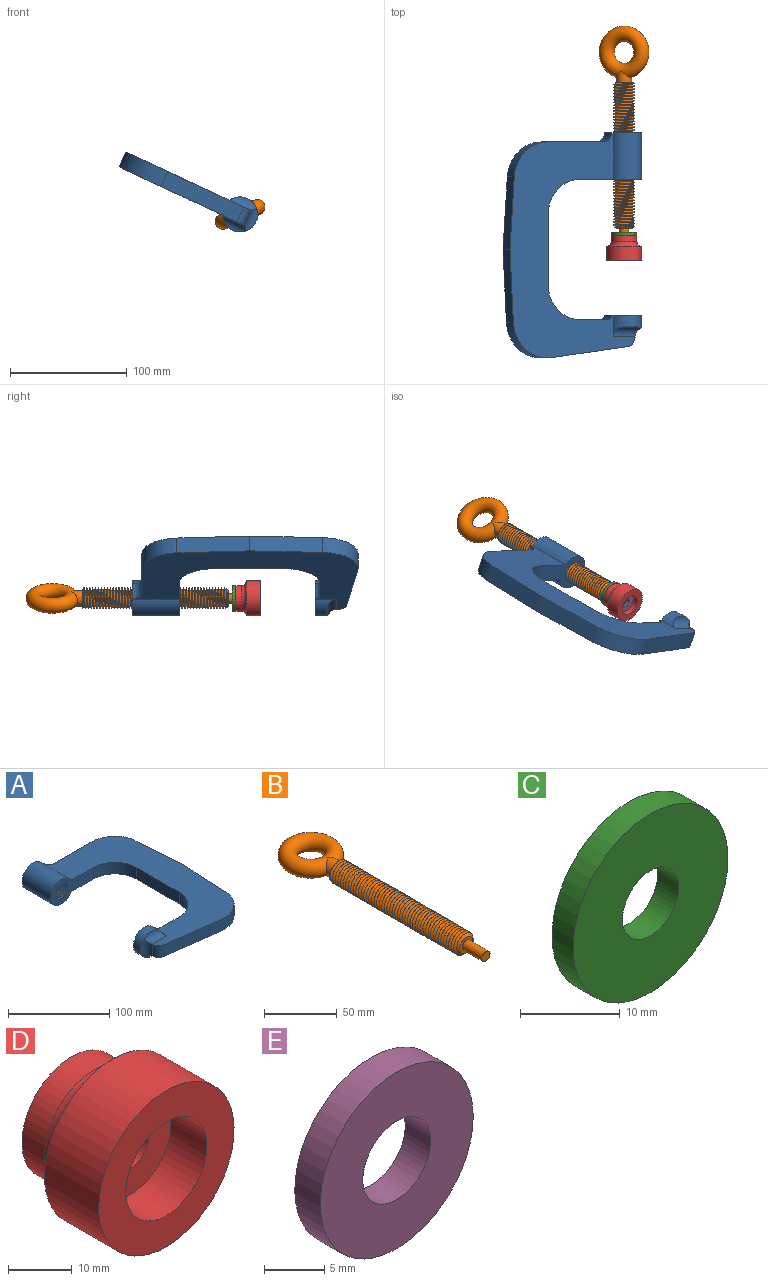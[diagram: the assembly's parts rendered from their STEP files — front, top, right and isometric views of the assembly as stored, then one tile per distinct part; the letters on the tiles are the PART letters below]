
ASSEMBLY  parts=5 mates=4
PART A: 26 faces, bbox 127.1x194.8x31.1 mm
  f0: cylinder r=15mm len=30mm, axis (0,1,0), area 973.5mm2, adj f5,f6,f7,f8,f24,f25
  f1: cylinder r=15mm len=40mm, axis (0,1,0), area 3187.3mm2, adj f3,f4,f7,f8
  f2: cylinder r=8mm len=14mm, axis (0,0,-1), area 168.5mm2, adj f6,f7,f8,f14
  f3: plane 61.09x31.09mm, normal (0,-1,0), area 911.6mm2, adj f1,f7,f8,f9,f21,f22,f23
  f4: plane 31.1x31.1mm, normal (0,1,0), area 491.6mm2, adj f1,f7,f8,f20,f21,f22,f23
  f5: plane 30x30mm, normal (0,1,0), area 714.8mm2, adj f0,f7,f8,f13
  f6: cylinder r=8mm len=21.21mm, axis (0,0,-1), area 206.8mm2, adj f0,f2,f7,f8,f24,f25
  f7: plane 192.73x118.03mm, normal (0,0,-1), area 10128.8mm2, adj f0,f1,f2,f3,f4,f5,f6,f9
  f8: plane 192.73x118.03mm, normal (0,0,1), area 10128.8mm2, adj f0,f1,f2,f3,f4,f5,f6,f9
  f9: cylinder r=30mm len=30mm, axis (0,0,-1), area 659.7mm2, adj f3,f7,f8,f10
  f10: plane 60x14mm, normal (-1,0,0), area 840mm2, adj f7,f8,f9,f11
  f11: cylinder r=30mm len=30mm, axis (0,0,-1), area 659.7mm2, adj f7,f8,f10,f12
  f12: plane 26x14mm, normal (0,1,0), area 364mm2, adj f7,f8,f11,f13
  f13: cylinder r=4mm len=14mm, axis (0,0,-1), area 88mm2, adj f5,f7,f8,f12
  f14: plane 71.71x14mm, normal (-0.13,-0.99,0), area 1012.7mm2, adj f2,f7,f8,f15
  f15: cylinder r=32mm len=36.15mm, axis (0,0,-1), area 739.5mm2, adj f7,f8,f14,f16
  f16: plane 62.38x14mm, normal (1,-0.05,0), area 874.5mm2, adj f7,f8,f15,f17
  f17: plane 62.08x14mm, normal (1,0.07,0), area 871mm2, adj f7,f8,f16,f18
  f18: cylinder r=32mm len=31.93mm, axis (0,0,-1), area 674.5mm2, adj f7,f8,f17,f19
  f19: plane 52.02x14mm, normal (0,1,0), area 728.3mm2, adj f7,f8,f18,f20
  f20: cylinder r=8mm len=14mm, axis (0,0,-1), area 175.9mm2, adj f4,f7,f8,f19
  f21: bspline ~41.89x16.58mm, area 1676.5mm2, adj f3,f4,f22,f23
  f22: bspline ~41.22x17.87mm, area 690.8mm2, adj f3,f4,f21,f23
  f23: bspline ~42.2x19.05mm, area 1678.2mm2, adj f3,f4,f21,f22
  f24: cylinder r=8mm len=23.87mm, axis (1,0,0), area 177.7mm2, adj f0,f6,f7
  f25: cylinder r=8mm len=23.87mm, axis (-1,0,0), area 177.7mm2, adj f0,f6,f8
PART B: 11 faces, bbox 50x195.7x19.3 mm
  f0: torus R=16mm, axis (0,0,-1), area 3935mm2, adj f1
  f1: cylinder r=6.5mm len=13mm, axis (0,-1,0), area 295.3mm2, adj f0,f5
  f2: cylinder r=4mm len=19mm, axis (0,-1,0), area 477.5mm2, adj f6,f7
  f3: cone r=6.5mm half-angle=45deg, axis (0,1,0), area 96.7mm2, adj f4,f7,f8,f9,f10
  f4: cylinder r=9mm len=122.5mm, axis (0,-1,0), area 168.2mm2, adj f3,f5,f9,f10
  f5: plane 17.36x17.33mm, normal (0,1,0), area 68.3mm2, adj f1,f4,f8,f9,f10
  f6: plane 8x8mm, normal (0,-1,0), area 50.3mm2, adj f2
  f7: plane 13x13mm, normal (0,-1,0), area 82.5mm2, adj f2,f3
  f8: bspline ~124.9x14.21mm, area 668.4mm2, adj f3,f5,f9,f10
  f9: bspline ~125.68x20.78mm, area 5481.3mm2, adj f3,f4,f5,f8
  f10: bspline ~126.93x20.78mm, area 5470.5mm2, adj f3,f4,f5,f8
PART C: 4 faces, bbox 22x3x22 mm
  f0: cylinder r=4mm len=8mm, axis (0,-1,0), area 75.4mm2, adj f2,f3
  f1: cylinder r=11mm len=22mm, axis (0,-1,0), area 207.3mm2, adj f2,f3
  f2: plane 22x22mm, normal (0,1,0), area 329.9mm2, adj f0,f1
  f3: plane 22x22mm, normal (0,-1,0), area 329.9mm2, adj f0,f1
PART D: 8 faces, bbox 32.5x21x32.5 mm
  f0: torus R=15mm, axis (0,-1,0), area 491.6mm2, adj f1,f4
  f1: cylinder r=15mm len=30mm, axis (0,-1,0), area 1131mm2, adj f0,f7
  f2: cylinder r=9mm len=18mm, axis (0,-1,0), area 452.4mm2, adj f6,f7
  f3: cylinder r=4mm len=13mm, axis (0,-1,0), area 326.7mm2, adj f5,f6
  f4: cylinder r=11mm len=22mm, axis (0,-1,0), area 345.6mm2, adj f0,f5
  f5: plane 22x22mm, normal (0,1,0), area 329.9mm2, adj f3,f4
  f6: plane 18x18mm, normal (0,-1,0), area 204.2mm2, adj f2,f3
  f7: plane 30x30mm, normal (0,-1,0), area 452.4mm2, adj f1,f2
PART E: 4 faces, bbox 18x3x18 mm
  f0: cylinder r=4mm len=8mm, axis (0,-1,0), area 75.4mm2, adj f2,f3
  f1: cylinder r=9mm len=18mm, axis (0,-1,0), area 169.6mm2, adj f2,f3
  f2: plane 18x18mm, normal (0,1,0), area 204.2mm2, adj f0,f1
  f3: plane 18x18mm, normal (0,-1,0), area 204.2mm2, adj f0,f1
PLACE A rot(axis=(0,-1,0),154.9deg) t=(-235.6,-17.64,9.01)mm fixed
PLACE B rot(axis=(0,-1,0),22.5deg) t=(-249.19,-118.97,15.37)mm
PLACE C rot(axis=(0,1,0),157.5deg) t=(-249.19,-105.97,15.37)mm
PLACE D rot(axis=(0,-1,0),112.5deg) t=(-249.19,-126.97,15.37)mm
PLACE E rot(axis=(0,1,0),67.5deg) t=(-249.19,-121.97,15.37)mm
MATE cylindrical D.f0 <-> A.f0  axis (0,-1,0) through (-249.19,-126.97,15.37)mm
MATE fastened D.f0 <-> E.f0  axis (0,-1,0) through (-249.19,-118.97,15.37)mm
MATE fastened D.f0 <-> B.f1  axis (0,-1,0) through (-249.19,-118.97,15.37)mm
MATE fastened D.f0 <-> C.f0  axis (0,1,0) through (-249.19,-105.97,15.37)mm
